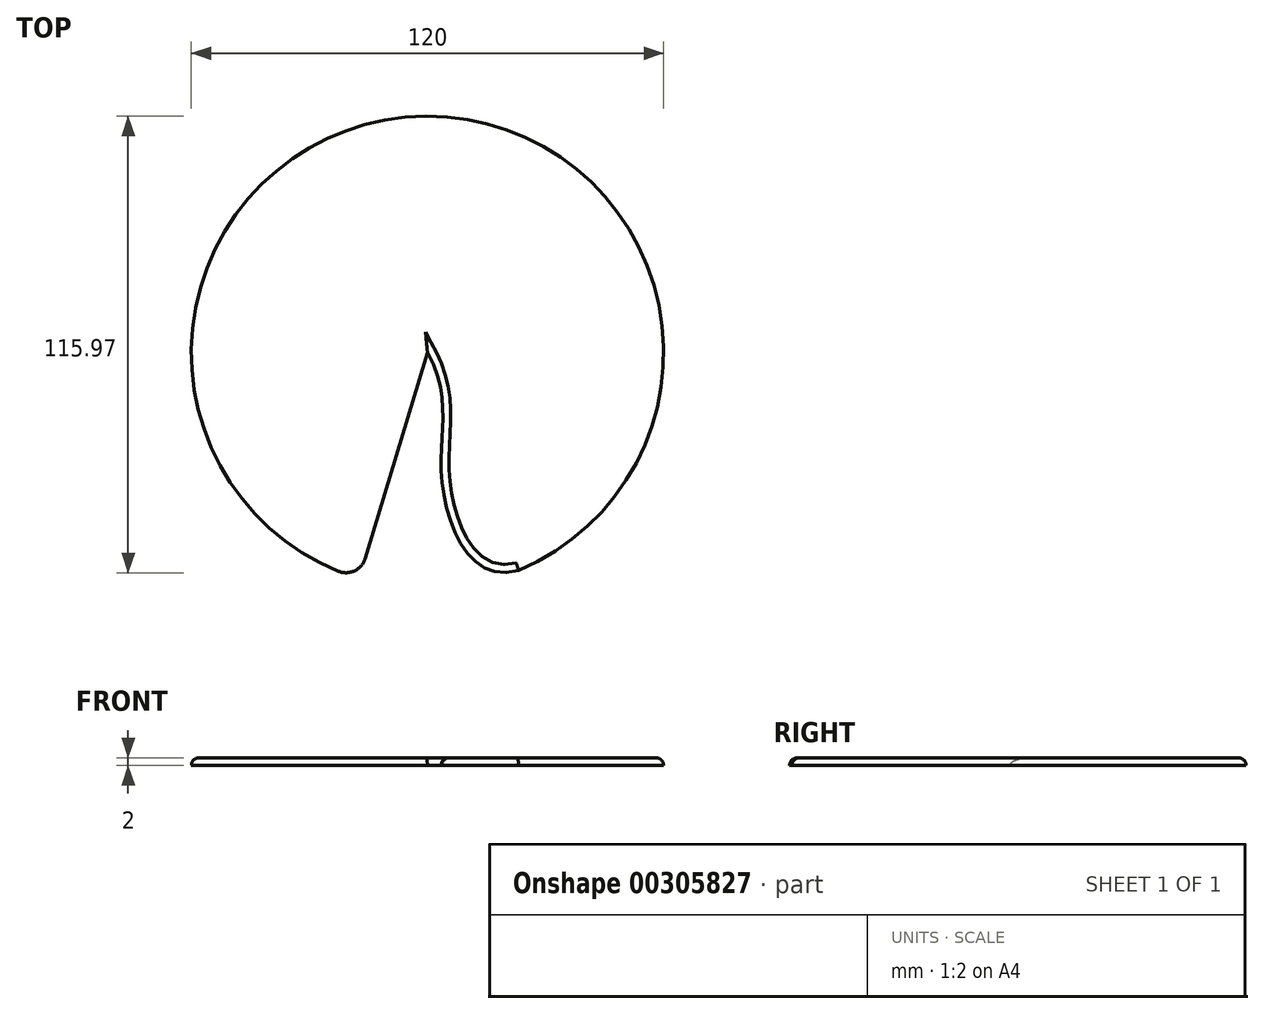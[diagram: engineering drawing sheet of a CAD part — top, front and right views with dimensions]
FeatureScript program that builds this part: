
annotation { "Feature Type Name" : "Feature", "Feature Type Description" : "" }
export const myFeature = defineFeature(function(context is Context, id is Id, definition is map)
    precondition{}
    {
        {
            var Q0;
            Q0=qCreatedBy(makeId("Top.planeOp"),FACE);
            var sketch = newSketch(context, id + "F0", { "sketchPlane" : qUnion([Q0])});
            skCircle(sketch, "E0", {"center": v(0, 0) * mm, "radius": 60 * mm});
            skLineSegment(sketch, "E1", {"start": v(-17.4, -57.42) * mm, "end": v(0, 0) * mm});
            skFitSpline(sketch, "E2", {"points": [v(0, 0) * mm, v(3.63, -32) * mm, v(23.18, -55.34) * mm], "startDerivative": vector(39.13, -73.66) * mm, "endDerivative": vector(77.83, 22.83) * mm});
            skSolve(sketch);
        }
        {
            var Q0;
            {var subQ0=sQuery(id+"F0.wireOp",EDGE,"E1");Q0=makeQuery(id+"F0.imprint","IMPRINT",FACE,{"disambiguationData":[TD([[makeQuery(id+"F0.imprint","IMPRINT",EDGE,{"derivedFrom":subQ0}),1.0]])]});}
            extrude(context, id + "F1", {"entities" : qUnion([Q0]), "depth" : 2 * mm});
        }
        {
            var Q0;
            Q0=makeQuery(id+"F1.opExtrude","SWEPT_EDGE",EDGE,{"disambiguationData":[OSD([sQuery(id+"F0.wireOp",EDGE,"E0"),sQuery(id+"F0.wireOp",EDGE,"E1")])]});
            fillet(context, id + "F2", {"entities" : qUnion([Q0]), "radius" : 5 * mm, "tangentPropagation" : true, "allowEdgeOverflow" : false});
        }
        {
            var Q0;
            Q0=makeQuery(id+"F1.opExtrude","CAP_EDGE",EDGE,{"disambiguationData":[OSD([sQuery(id+"F0.wireOp",EDGE,"E0")])],"isStart":false});
            var Q1;
            Q1=makeQuery(id+"F1.opExtrude","CAP_EDGE",EDGE,{"disambiguationData":[OSD([sQuery(id+"F0.wireOp",EDGE,"E2")])],"isStart":false});
            var Q2;
            {var subQ0=sQuery(id+"F0.wireOp",EDGE,"E1");var subQ1=sQuery(id+"F0.wireOp",EDGE,"E0");Q2=makeQuery(id+"F2.opFillet","BLEND_EDGE",EDGE,{"blendedFrom":[makeQuery(id+"F1.opExtrude","SWEPT_EDGE",EDGE,{"disambiguationData":[OSD([subQ1,subQ0])]}),makeQuery(id+"F1.opExtrude","CAP_FACE",FACE,{"disambiguationData":[OSD([subQ1,subQ0,sQuery(id+"F0.wireOp",EDGE,"E2")])],"isStart":false})],"blendedInto":[makeQuery(id+"F1.opExtrude","CAP_FACE",FACE,{"disambiguationData":[OSD([subQ1,subQ0,sQuery(id+"F0.wireOp",EDGE,"E2")])],"isStart":false})]});}
            fillet(context, id + "F3", {"entities" : qUnion([Q0, Q1, Q2]), "radius" : 2 * mm, "tangentPropagation" : true, "allowEdgeOverflow" : false});
        }
    });
